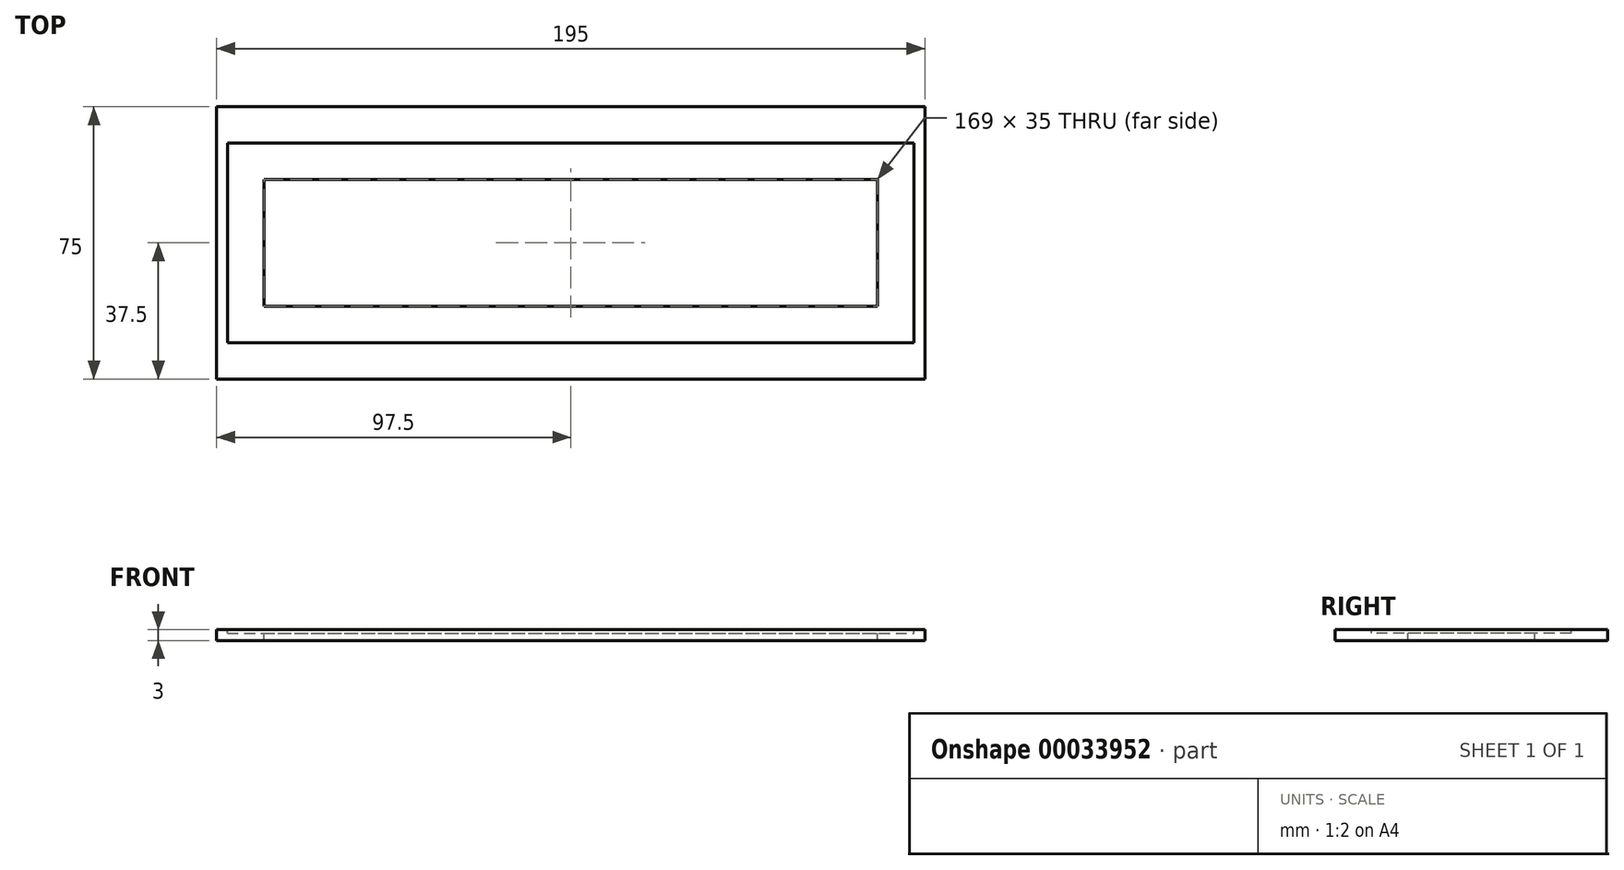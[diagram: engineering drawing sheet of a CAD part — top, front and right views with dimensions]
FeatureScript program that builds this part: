
annotation { "Feature Type Name" : "Feature", "Feature Type Description" : "" }
export const myFeature = defineFeature(function(context is Context, id is Id, definition is map)
    precondition{}
    {
        {
            var Q0;
            Q0=qCreatedBy(makeId("Top.planeOp"),FACE);
            var sketch = newSketch(context, id + "F0", { "sketchPlane" : qUnion([Q0])});
            skLineSegment(sketch, "E0.bottom", {"start": v(0, 0) * mm, "end": v(195, 0) * mm});
            skLineSegment(sketch, "E0.top", {"start": v(0, -75) * mm, "end": v(195, -75) * mm});
            skLineSegment(sketch, "E0.left", {"start": v(0, 0) * mm, "end": v(0, -75) * mm});
            skLineSegment(sketch, "E0.right", {"start": v(195, 0) * mm, "end": v(195, -75) * mm});
            skSolve(sketch);
        }
        {
            var Q0;
            Q0 = qSketchRegion(id + "F0", true);
            extrude(context, id + "F1", {"entities" : qUnion([Q0]), "depth" : 3 * mm, "offsetDistance" : 25 * mm});
        }
        {
            var Q0;
            Q0=makeQuery(id+"F1.opExtrude","CAP_FACE",FACE,{"disambiguationData":[OSD([sQuery(id+"F0.wireOp",EDGE,"E0.bottom"),sQuery(id+"F0.wireOp",EDGE,"E0.top"),sQuery(id+"F0.wireOp",EDGE,"E0.left"),sQuery(id+"F0.wireOp",EDGE,"E0.right")])],"isStart":false});
            var sketch = newSketch(context, id + "F2", { "sketchPlane" : qUnion([Q0])});
            skLineSegment(sketch, "E1.bottom", {"start": v(3, -10) * mm, "end": v(192, -10) * mm});
            skLineSegment(sketch, "E1.top", {"start": v(3, -65) * mm, "end": v(192, -65) * mm});
            skLineSegment(sketch, "E1.left", {"start": v(3, -10) * mm, "end": v(3, -65) * mm});
            skLineSegment(sketch, "E1.right", {"start": v(192, -10) * mm, "end": v(192, -65) * mm});
            skSolve(sketch);
        }
        {
            var Q0;
            Q0 = qSketchRegion(id + "F2", true);
            extrude(context, id + "F3", {"entities" : qUnion([Q0]), "operationType" : NewBodyOperationType.REMOVE, "oppositeDirection" : true, "depth" : 1 * mm, "offsetDistance" : 25 * mm});
        }
        {
            var Q0;
            Q0=makeQuery(id+"F3.boolean.opBoolean","COPY",FACE,{"derivedFrom":makeQuery(id+"F3.opExtrude","CAP_FACE",FACE,{"disambiguationData":[OSD([sQuery(id+"F2.wireOp",EDGE,"E1.bottom"),sQuery(id+"F2.wireOp",EDGE,"E1.top"),sQuery(id+"F2.wireOp",EDGE,"E1.left"),sQuery(id+"F2.wireOp",EDGE,"E1.right")])],"isStart":false})});
            var sketch = newSketch(context, id + "F4", { "sketchPlane" : qUnion([Q0])});
            skLineSegment(sketch, "E2.bottom", {"start": v(13, -20) * mm, "end": v(182, -20) * mm});
            skLineSegment(sketch, "E2.top", {"start": v(13, -55) * mm, "end": v(182, -55) * mm});
            skLineSegment(sketch, "E2.left", {"start": v(13, -20) * mm, "end": v(13, -55) * mm});
            skLineSegment(sketch, "E2.right", {"start": v(182, -20) * mm, "end": v(182, -55) * mm});
            skSolve(sketch);
        }
        {
            var Q0;
            Q0 = qSketchRegion(id + "F4", true);
            extrude(context, id + "F5", {"entities" : qUnion([Q0]), "operationType" : NewBodyOperationType.REMOVE, "oppositeDirection" : true, "depth" : 25 * mm, "offsetDistance" : 25 * mm});
        }
    });
